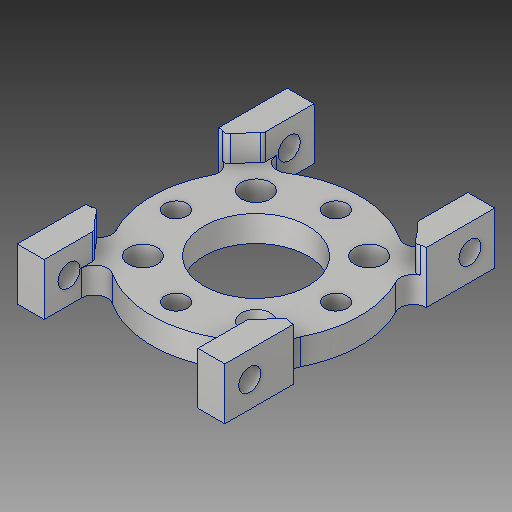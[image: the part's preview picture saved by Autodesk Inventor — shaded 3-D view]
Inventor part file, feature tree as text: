
AUTODESK INVENTOR PART (.ipt)
format: ipt  version: 2019 (Build 230136000, 136)  size: 192,512 bytes
history: native  units: in
note: dims shown in document units (in); Inventor stores cm internally (conversion verified against a paired STEP export)
features: mirror x1
ambient origin geometry x8: Origin, YZ Plane, XZ Plane, XY Plane, X Axis, Y Axis, Z Axis, Center Point
bodies: Solid1 (feature_tree)
feature tree (1):
  mirror  "Mirror6"
